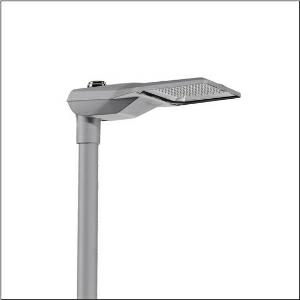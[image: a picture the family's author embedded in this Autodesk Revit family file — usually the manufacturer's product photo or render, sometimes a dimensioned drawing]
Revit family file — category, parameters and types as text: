
# Revit family: streetlight_sl_21_midi___p1_0a_5xe7a37n08lb_cb5e
name_source: partatom
category: Lighting Fixtures
units: mm (PartAtom-declared; Revit-internal decimal feet)

## family parameters
Cut with Voids When Loaded = No
Host = Face
Light Source = No
Part Type = Normal
Room Calculation Point = No
Round Connector Dimension = Use Diameter
Shared = No

## types (1)
- --- (1 x LED, 14340 lm, 98.3 W, 3000K)
    Apparent Load = 98 VA
    CIE Flux Codes = 21 50 90 100 100
    Color Rendering = 70
    Color Temperature = 3000K
    Default Elevation = 1800 mm
    Description = Streetlight SL 21 midi, mast luminaire, primary light control with lens, of PMMA, primary optical cover: cover, of toughened safety glass, transparent, light distribution: P1.0a, light emission: direct distribution, primary light characteristic: asymmetric, installation type: side-entry, LED, 3G 2.5mm², High Power LED, rated luminous flux: 14.340lm, luminous efficacy: 146lm/W, light colour: 730, colour temperature: 3000K, control gear: NEMA (7pin), control: overheat protection, pre-setting: linear dimming characteristic, constant luminous flux control, time-dependent luminous flux control, flexible luminous flux parameterisation, mains connection: 220..240V, AC, 50/60Hz, connection cable pre-assembled, cable length: 10,5m, wiring characteristics: H05VV-F, start of lifetime: 98W, end of service life: 101W, reduction: 45W, luminaire housing, of diecast aluminium (EN AC-44300), powder-coated, SITECO metallic grey (DB 702S), corrosivity category C5 high according to DIN EN ISO 12944, multi-level sealing system, sealing non-destructively replaceable, inclination adjustable: 0°, 5°, 10°, 15°, length: 644mm, width: 335mm, height: 110mm, spigot size: 42mm (side-entry), mounting height: 4..8m, protection rating (complete): IP66, insulation class (complete): insulation class I (protective earthing), certification: CE, ENEC, ENEC+, VDE, impact resistance: IK10, permissible operating ambient temperature for outdoor applications: -40..+50°C, standard-compliant lighting for roads and squares, packaging unit: 1 piece

Light Distribution: P1.0a
    Height = 111 mm
    Lamp = 1 x LED
    Lamp Light Flux = 14340 lm
    Lamp Power = 98.3 W
    Lamp count = 1
    Length = 644 mm
    Luminous efficacy = 146 lm/W
    Manufacturer = Siteco
    ModVariant = No
    Model = 5XE7A37N08LB
    Number of Poles = 1
    OnlyDefault = Yes
    Power Factor = 1
    Product Name = Streetlight SL 21 midi | P1.0a
    Product group = mast luminaire | pylon top
    ProductGroupID = 6100
    Protection Class = Protection class I
    Protection Degree = IP 66
    RLX_Detail_Level = 1
    RLX_Emergency_Light_Flux = 0 lm
    RLX_Emergency_Type = 0
    RLX_Emergency_Type_DB = No
    RlxData = <blob elided: 37893 chars, md5=57843d1c>
    Socket = socket
    Standby Power = 0 W
    System Light Flux = 14340 lm
    System Power = 98 W
    Type Comments = factory setting: luminous flux: 100 % | dim-lin: 254 | 1020 mA
    Type Image = l_1294377.jpg
    URL = http://relux.com
    VarID = @adj_134055
    Voltage = 0 V
    Weight = 0.00 kg
    Width = 336 mm

## geometry (parser evidence)
native form markers: Blend x4, Sweep x10
no freeform markers — native parametric forms only
